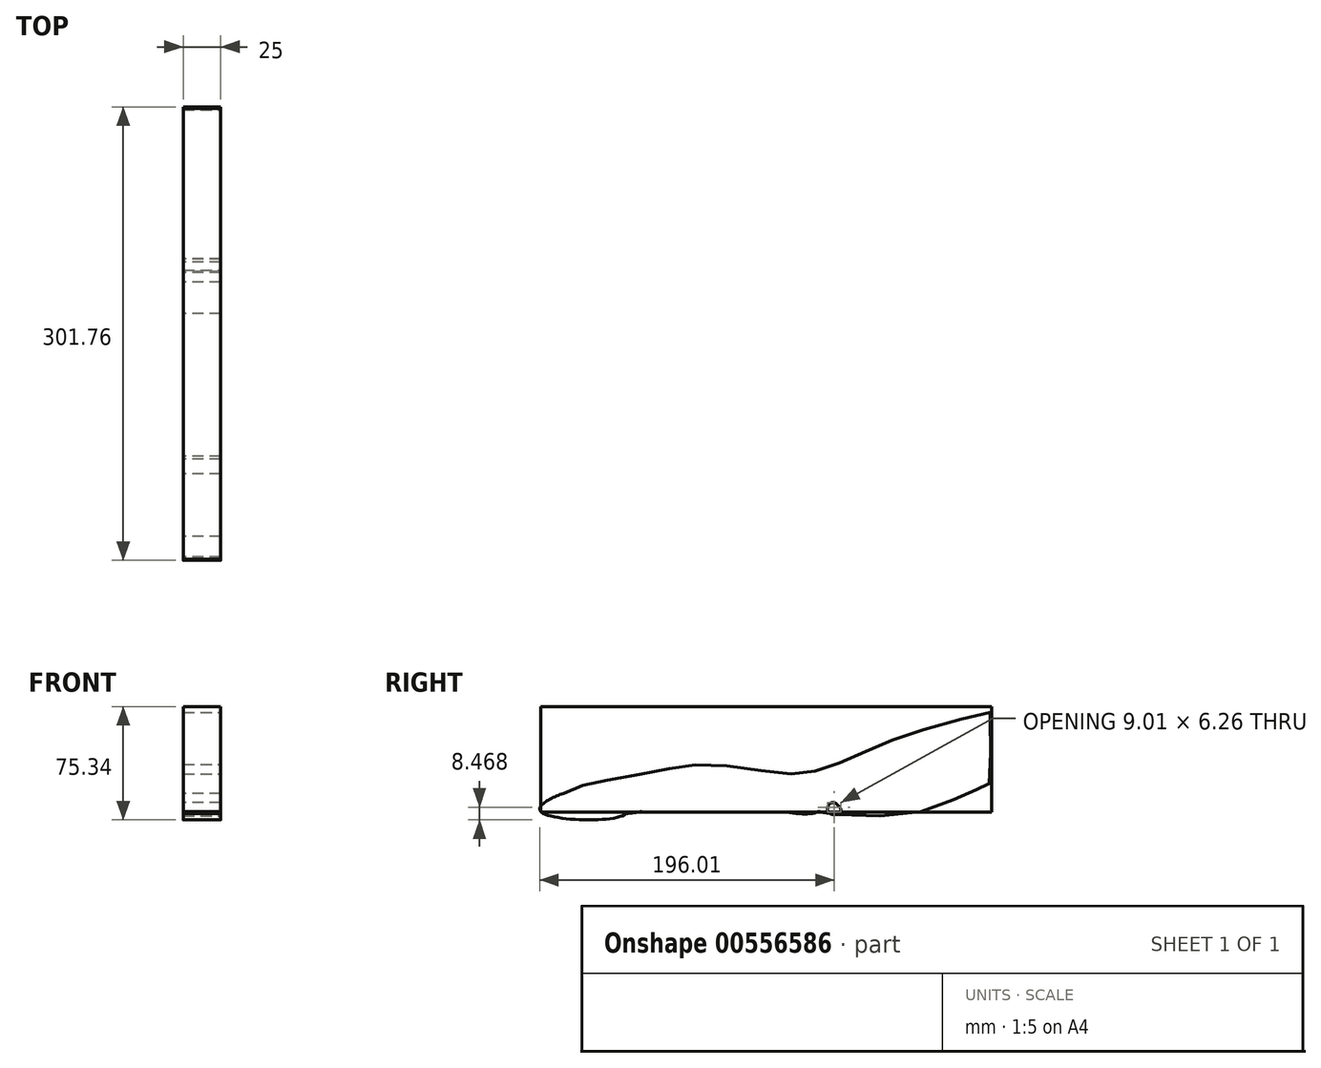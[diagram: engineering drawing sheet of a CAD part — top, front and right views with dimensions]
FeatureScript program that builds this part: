
annotation { "Feature Type Name" : "Feature", "Feature Type Description" : "" }
export const myFeature = defineFeature(function(context is Context, id is Id, definition is map)
    precondition{}
    {
        {
            var Q0;
            Q0=qCreatedBy(makeId("Right.planeOp"),FACE);
            var sketch = newSketch(context, id + "F0", { "sketchPlane" : qUnion([Q0])});
            skLineSegment(sketch, "E0.bottom", {"start": v(164.2, 50.84) * mm, "end": v(-135.8, 50.84) * mm});
            skLineSegment(sketch, "E0.top", {"start": v(164.2, -19.16) * mm, "end": v(-135.8, -19.16) * mm});
            skLineSegment(sketch, "E0.left", {"start": v(164.2, 50.84) * mm, "end": v(164.2, -19.16) * mm});
            skLineSegment(sketch, "E0.right", {"start": v(-135.8, 50.84) * mm, "end": v(-135.8, -19.16) * mm});
            skPoint(sketch, "E0.middle", {"position": v(14.2, 15.84) * mm});
            skSolve(sketch);
        }
        {
            var Q0;
            Q0=makeQuery(id+"F0.imprint","IMPRINT",FACE,{"disambiguationData":[TD([[makeQuery(id+"F0.imprint","IMPRINT",EDGE,{"derivedFrom":sQuery(id+"F0.wireOp",EDGE,"E0.bottom")}),1.0]])]});
            var sketch = newSketch(context, id + "F1", { "sketchPlane" : qUnion([Q0])});
            skSolve(sketch);
        }
        {
            var Q0;
            Q0=makeQuery(id+"F1.imprint","IMPRINT",FACE,{"disambiguationData":[TD([[makeQuery(id+"F1.imprint","IMPRINT",EDGE,{"derivedFrom":makeQuery(id+"F0.imprint","IMPRINT",EDGE,{"derivedFrom":sQuery(id+"F0.wireOp",EDGE,"E0.bottom")})}),1.0]])]});
            var sketch = newSketch(context, id + "F2", { "sketchPlane" : qUnion([Q0])});
            skFitSpline(sketch, "E1", {"points": [v(-135.83, -18.87) * mm, v(-120.6, -6.78) * mm, v(-101.8, 0) * mm, v(-59.7, 7.55) * mm, v(-26.1, 12.48) * mm, v(23.61, 6.66) * mm, v(50.49, 8.9) * mm, v(82.29, 21.89) * mm, v(125.28, 37.56) * mm, v(165.14, 46.97) * mm, v(163.8, 43.83) * mm, v(162.9, 0) * mm, v(154.84, -4.1) * mm, v(120.8, -17.98) * mm, v(48.7, -18.87) * mm, v(9.73, -11.7) * mm, v(-60.59, -17.53) * mm, v(-78.95, -20.22) * mm, v(-135.83, -18.87) * mm]});
            skFitSpline(sketch, "E2", {"points": [v(-120.6, -6.78) * mm, v(-135.83, -18.87) * mm, v(-78.95, -20.22) * mm, v(-90.15, -6.78) * mm, v(-120.6, -6.78) * mm]});
            skFitSpline(sketch, "E3", {"points": [v(9.73, -11.7) * mm, v(41.53, -6.78) * mm, v(48.7, -18.87) * mm, v(9.73, -11.7) * mm]});
            skFitSpline(sketch, "E4", {"points": [v(0, 0) * mm, v(38.4, 0) * mm, v(75.12, 6.66) * mm, v(116.32, 21.89) * mm, v(156.63, 33.98) * mm, v(156.19, 34.43) * mm, v(157.98, 34.87) * mm], "startDerivative": vector(170.88, -5.84) * mm, "endDerivative": vector(56.58, 7.65) * mm});
            skFitSpline(sketch, "E5", {"points": [v(50.49, -6.78) * mm, v(77.36, 0) * mm, v(118.56, 13.38) * mm, v(155.3, 18.75) * mm], "startDerivative": vector(86.35, 18.62) * mm, "endDerivative": vector(105.57, 9.52) * mm});
            skFitSpline(sketch, "E6", {"points": [v(-71.4, -17.53) * mm, v(-65.65, -18.4) * mm, v(-65.62, -10.51) * mm, v(-72.36, -10.51) * mm, v(-71.4, -17.53) * mm]});
            skFitSpline(sketch, "E7", {"points": [v(55.34, -18.87) * mm, v(57.75, -12.92) * mm, v(64.01, -17.53) * mm, v(62.09, -20.74) * mm, v(55.34, -18.87) * mm]});
            skSolve(sketch);
        }
        {
            var Q0;
            {var subQ0=sQuery(id+"F2.wireOp",EDGE,"E7");var subQ1=sQuery(id+"F2.wireOp",EDGE,"E1");var subQ2=makeQuery(id+"F2.imprint","INTERSECT",VERTEX,{"disambiguationData":[OD(0.0)],"derivedFrom":[subQ1,subQ0]});Q0=makeQuery(id+"F2.imprint","IMPRINT",FACE,{"disambiguationData":[TD([[makeQuery(id+"F2.imprint","IMPRINT",EDGE,{"disambiguationData":[TD([[subQ2,-1.0]])],"derivedFrom":subQ1}),1.0]])]});}
            var Q1;
            {var subQ0=sQuery(id+"F2.wireOp",EDGE,"E2");var subQ1=sQuery(id+"F2.wireOp",EDGE,"E1");var subQ2=makeQuery(id+"F2.imprint","INTERSECT",VERTEX,{"disambiguationData":[OD(1.0)],"derivedFrom":[subQ1,subQ0]});Q1=makeQuery(id+"F2.imprint","IMPRINT",FACE,{"disambiguationData":[TD([[makeQuery(id+"F2.imprint","IMPRINT",EDGE,{"disambiguationData":[TD([[subQ2,-1.0]])],"derivedFrom":subQ1}),1.0]])]});}
            var Q2;
            {var subQ0=sQuery(id+"F2.wireOp",EDGE,"E3");var subQ1=sQuery(id+"F2.wireOp",EDGE,"E1");var subQ2=makeQuery(id+"F2.imprint","INTERSECT",VERTEX,{"disambiguationData":[OD(0.0)],"derivedFrom":[subQ1,subQ0]});Q2=makeQuery(id+"F2.imprint","IMPRINT",FACE,{"disambiguationData":[TD([[makeQuery(id+"F2.imprint","IMPRINT",EDGE,{"disambiguationData":[TD([[subQ2,-1.0]])],"derivedFrom":subQ1}),-1.0]])]});}
            var Q3;
            {var subQ0=sQuery(id+"F2.wireOp",EDGE,"E6");var subQ1=sQuery(id+"F2.wireOp",EDGE,"E1");var subQ2=makeQuery(id+"F2.imprint","INTERSECT",VERTEX,{"disambiguationData":[OD(0.0)],"derivedFrom":[subQ1,subQ0]});Q3=makeQuery(id+"F2.imprint","IMPRINT",FACE,{"disambiguationData":[TD([[makeQuery(id+"F2.imprint","IMPRINT",EDGE,{"disambiguationData":[TD([[subQ2,-1.0]])],"derivedFrom":subQ1}),-1.0]])]});}
            var Q4;
            {var subQ0=sQuery(id+"F2.wireOp",EDGE,"E1");var subQ1=makeQuery(id+"F1.imprint","IMPRINT",EDGE,{"derivedFrom":makeQuery(id+"F0.imprint","IMPRINT",EDGE,{"derivedFrom":sQuery(id+"F0.wireOp",EDGE,"E0.left")})});var subQ2=makeQuery(id+"F2.imprint","INTERSECT",VERTEX,{"disambiguationData":[OD(0.0)],"derivedFrom":[subQ1,subQ0]});Q4=makeQuery(id+"F2.imprint","IMPRINT",FACE,{"disambiguationData":[TD([[makeQuery(id+"F2.imprint","IMPRINT",EDGE,{"disambiguationData":[TD([[subQ2,-1.0]])],"derivedFrom":subQ0}),-1.0]])]});}
            var Q5;
            {var subQ0=sQuery(id+"F2.wireOp",EDGE,"E3");var subQ1=makeQuery(id+"F1.imprint","IMPRINT",EDGE,{"derivedFrom":makeQuery(id+"F0.imprint","IMPRINT",EDGE,{"derivedFrom":sQuery(id+"F0.wireOp",EDGE,"E0.top")})});var subQ2=makeQuery(id+"F2.imprint","INTERSECT",VERTEX,{"disambiguationData":[OD(0.0)],"derivedFrom":[subQ1,subQ0]});Q5=makeQuery(id+"F2.imprint","IMPRINT",FACE,{"disambiguationData":[TD([[makeQuery(id+"F2.imprint","IMPRINT",EDGE,{"disambiguationData":[TD([[subQ2,-1.0]])],"derivedFrom":subQ0}),-1.0]])]});}
            var Q6;
            {var subQ0=sQuery(id+"F2.wireOp",EDGE,"E6");var subQ1=makeQuery(id+"F1.imprint","IMPRINT",EDGE,{"derivedFrom":makeQuery(id+"F0.imprint","IMPRINT",EDGE,{"derivedFrom":sQuery(id+"F0.wireOp",EDGE,"E0.top")})});var subQ2=makeQuery(id+"F2.imprint","INTERSECT",VERTEX,{"disambiguationData":[OD(0.0)],"derivedFrom":[subQ1,subQ0]});Q6=makeQuery(id+"F2.imprint","IMPRINT",FACE,{"disambiguationData":[TD([[makeQuery(id+"F2.imprint","IMPRINT",EDGE,{"disambiguationData":[TD([[subQ2,-1.0]])],"derivedFrom":subQ0}),1.0]])]});}
            var Q7;
            {var subQ0=sQuery(id+"F2.wireOp",EDGE,"E2");var subQ1=sQuery(id+"F2.wireOp",EDGE,"E1");var subQ2=makeQuery(id+"F2.imprint","INTERSECT",VERTEX,{"disambiguationData":[OD(0.0)],"derivedFrom":[subQ1,subQ0]});Q7=makeQuery(id+"F2.imprint","IMPRINT",FACE,{"disambiguationData":[TD([[makeQuery(id+"F2.imprint","IMPRINT",EDGE,{"disambiguationData":[TD([[subQ2,-1.0]])],"derivedFrom":subQ1}),1.0]])]});}
            var Q8;
            {var subQ0=sQuery(id+"F2.wireOp",EDGE,"E7");var subQ1=sQuery(id+"F2.wireOp",EDGE,"E1");var subQ2=makeQuery(id+"F2.imprint","INTERSECT",VERTEX,{"disambiguationData":[OD(0.0)],"derivedFrom":[subQ1,subQ0]});Q8=makeQuery(id+"F2.imprint","IMPRINT",FACE,{"disambiguationData":[TD([[makeQuery(id+"F2.imprint","IMPRINT",EDGE,{"disambiguationData":[TD([[subQ2,1.0]])],"derivedFrom":subQ1}),-1.0]])]});}
            var Q9;
            {var subQ0=sQuery(id+"F2.wireOp",EDGE,"E7");var subQ1=sQuery(id+"F2.wireOp",EDGE,"E1");var subQ2=makeQuery(id+"F2.imprint","INTERSECT",VERTEX,{"disambiguationData":[OD(1.0)],"derivedFrom":[subQ1,subQ0]});Q9=makeQuery(id+"F2.imprint","IMPRINT",FACE,{"disambiguationData":[TD([[makeQuery(id+"F2.imprint","IMPRINT",EDGE,{"disambiguationData":[TD([[subQ2,-1.0]])],"derivedFrom":subQ1}),-1.0]])]});}
            var Q10;
            {var subQ0=sQuery(id+"F2.wireOp",EDGE,"E2");var subQ1=sQuery(id+"F2.wireOp",EDGE,"E1");var subQ2=makeQuery(id+"F2.imprint","INTERSECT",VERTEX,{"disambiguationData":[OD(1.0)],"derivedFrom":[subQ1,subQ0]});Q10=makeQuery(id+"F2.imprint","IMPRINT",FACE,{"disambiguationData":[TD([[makeQuery(id+"F2.imprint","IMPRINT",EDGE,{"disambiguationData":[TD([[subQ2,1.0]])],"derivedFrom":subQ1}),-1.0]])]});}
            var Q11;
            {var subQ0=sQuery(id+"F2.wireOp",EDGE,"E2");var subQ1=sQuery(id+"F2.wireOp",EDGE,"E1");var subQ2=makeQuery(id+"F2.imprint","INTERSECT",VERTEX,{"disambiguationData":[OD(2.0)],"derivedFrom":[subQ1,subQ0]});Q11=makeQuery(id+"F2.imprint","IMPRINT",FACE,{"disambiguationData":[TD([[makeQuery(id+"F2.imprint","IMPRINT",EDGE,{"disambiguationData":[TD([[subQ2,-1.0]])],"derivedFrom":subQ1}),-1.0]])]});}
            var Q12;
            {var subQ0=sQuery(id+"F2.wireOp",EDGE,"E2");var subQ1=sQuery(id+"F2.wireOp",EDGE,"E1");var subQ2=makeQuery(id+"F2.imprint","INTERSECT",VERTEX,{"disambiguationData":[OD(0.0)],"derivedFrom":[subQ1,subQ0]});Q12=makeQuery(id+"F2.imprint","IMPRINT",FACE,{"disambiguationData":[TD([[makeQuery(id+"F2.imprint","IMPRINT",EDGE,{"disambiguationData":[TD([[subQ2,1.0]])],"derivedFrom":subQ1}),-1.0]])]});}
            var Q13;
            {var subQ0=sQuery(id+"F2.wireOp",EDGE,"E7");var subQ1=makeQuery(id+"F1.imprint","IMPRINT",EDGE,{"derivedFrom":makeQuery(id+"F0.imprint","IMPRINT",EDGE,{"derivedFrom":sQuery(id+"F0.wireOp",EDGE,"E0.top")})});var subQ2=makeQuery(id+"F2.imprint","INTERSECT",VERTEX,{"disambiguationData":[OD(0.0)],"derivedFrom":[subQ1,subQ0]});Q13=makeQuery(id+"F2.imprint","IMPRINT",FACE,{"disambiguationData":[TD([[makeQuery(id+"F2.imprint","IMPRINT",EDGE,{"disambiguationData":[TD([[subQ2,1.0]])],"derivedFrom":subQ0}),-1.0]])]});}
            var Q14;
            {var subQ0=sQuery(id+"F2.wireOp",EDGE,"E2");var subQ1=sQuery(id+"F2.wireOp",EDGE,"E1");var subQ2=makeQuery(id+"F2.imprint","INTERSECT",VERTEX,{"disambiguationData":[OD(0.0)],"derivedFrom":[subQ1,subQ0]});Q14=makeQuery(id+"F2.imprint","IMPRINT",FACE,{"disambiguationData":[TD([[makeQuery(id+"F2.imprint","IMPRINT",EDGE,{"disambiguationData":[TD([[subQ2,-1.0]])],"derivedFrom":subQ1}),-1.0]])]});}
            var Q15;
            {var subQ0=sQuery(id+"F2.wireOp",EDGE,"E2");var subQ1=sQuery(id+"F2.wireOp",EDGE,"E1");var subQ2=makeQuery(id+"F2.imprint","INTERSECT",VERTEX,{"disambiguationData":[OD(3.0)],"derivedFrom":[subQ1,subQ0]});Q15=makeQuery(id+"F2.imprint","IMPRINT",FACE,{"disambiguationData":[TD([[makeQuery(id+"F2.imprint","IMPRINT",EDGE,{"disambiguationData":[TD([[subQ2,1.0]])],"derivedFrom":subQ1}),1.0]])]});}
            var Q16;
            {var subQ0=sQuery(id+"F2.wireOp",EDGE,"E7");var subQ1=sQuery(id+"F2.wireOp",EDGE,"E1");var subQ2=makeQuery(id+"F2.imprint","INTERSECT",VERTEX,{"disambiguationData":[OD(0.0)],"derivedFrom":[subQ1,subQ0]});Q16=makeQuery(id+"F2.imprint","IMPRINT",FACE,{"disambiguationData":[TD([[makeQuery(id+"F2.imprint","IMPRINT",EDGE,{"disambiguationData":[TD([[subQ2,-1.0]])],"derivedFrom":subQ1}),-1.0]])]});}
            var Q17;
            {var subQ0=sQuery(id+"F2.wireOp",EDGE,"E3");var subQ1=sQuery(id+"F2.wireOp",EDGE,"E1");var subQ2=makeQuery(id+"F2.imprint","INTERSECT",VERTEX,{"disambiguationData":[OD(0.0)],"derivedFrom":[subQ1,subQ0]});Q17=makeQuery(id+"F2.imprint","IMPRINT",FACE,{"disambiguationData":[TD([[makeQuery(id+"F2.imprint","IMPRINT",EDGE,{"disambiguationData":[TD([[subQ2,-1.0]])],"derivedFrom":subQ1}),1.0]])]});}
            var Q18;
            {var subQ0=sQuery(id+"F2.wireOp",EDGE,"E6");var subQ1=sQuery(id+"F2.wireOp",EDGE,"E1");var subQ2=makeQuery(id+"F2.imprint","INTERSECT",VERTEX,{"disambiguationData":[OD(0.0)],"derivedFrom":[subQ1,subQ0]});Q18=makeQuery(id+"F2.imprint","IMPRINT",FACE,{"disambiguationData":[TD([[makeQuery(id+"F2.imprint","IMPRINT",EDGE,{"disambiguationData":[TD([[subQ2,-1.0]])],"derivedFrom":subQ1}),1.0]])]});}
            var Q19;
            {var subQ0=sQuery(id+"F2.wireOp",EDGE,"E2");var subQ1=sQuery(id+"F2.wireOp",EDGE,"E1");var subQ2=makeQuery(id+"F2.imprint","INTERSECT",VERTEX,{"disambiguationData":[OD(1.0)],"derivedFrom":[subQ1,subQ0]});Q19=makeQuery(id+"F2.imprint","IMPRINT",FACE,{"disambiguationData":[TD([[makeQuery(id+"F2.imprint","IMPRINT",EDGE,{"disambiguationData":[TD([[subQ2,-1.0]])],"derivedFrom":subQ1}),-1.0]])]});}
            var Q20;
            {var subQ0=sQuery(id+"F2.wireOp",EDGE,"E1");var subQ1=makeQuery(id+"F1.imprint","IMPRINT",EDGE,{"derivedFrom":makeQuery(id+"F0.imprint","IMPRINT",EDGE,{"derivedFrom":sQuery(id+"F0.wireOp",EDGE,"E0.top")})});var subQ2=makeQuery(id+"F2.imprint","INTERSECT",VERTEX,{"disambiguationData":[OD(3.0)],"derivedFrom":[subQ1,subQ0]});Q20=makeQuery(id+"F2.imprint","IMPRINT",FACE,{"disambiguationData":[TD([[makeQuery(id+"F2.imprint","IMPRINT",EDGE,{"disambiguationData":[TD([[subQ2,-1.0]])],"derivedFrom":subQ0}),-1.0]])]});}
            var Q21;
            {var subQ0=sQuery(id+"F2.wireOp",EDGE,"E2");var subQ4=sQuery(id+"F2.wireOp",EDGE,"E1");var subQ5=makeQuery(id+"F2.imprint","INTERSECT",VERTEX,{"disambiguationData":[OD(3.0)],"derivedFrom":[subQ4,subQ0]});Q21=makeQuery(id+"F2.imprint","IMPRINT",FACE,{"disambiguationData":[TD([[makeQuery(id+"F2.imprint","IMPRINT",EDGE,{"disambiguationData":[TD([[subQ5,1.0]])],"derivedFrom":subQ4}),-1.0]])]});}
            var Q22;
            {var subQ1=sQuery(id+"F2.wireOp",EDGE,"E1");var subQ6=sQuery(id+"F2.wireOp",EDGE,"E2");var subQ7=makeQuery(id+"F2.imprint","INTERSECT",VERTEX,{"disambiguationData":[OD(3.0)],"derivedFrom":[subQ1,subQ6]});Q22=makeQuery(id+"F2.imprint","IMPRINT",FACE,{"disambiguationData":[TD([[makeQuery(id+"F2.imprint","IMPRINT",EDGE,{"disambiguationData":[TD([[subQ7,-1.0]])],"derivedFrom":subQ1}),-1.0]])]});}
            var Q23;
            {var subQ0=sQuery(id+"F2.wireOp",EDGE,"E3");var subQ1=sQuery(id+"F2.wireOp",EDGE,"E1");var subQ2=makeQuery(id+"F2.imprint","INTERSECT",VERTEX,{"disambiguationData":[OD(1.0)],"derivedFrom":[subQ1,subQ0]});Q23=makeQuery(id+"F2.imprint","IMPRINT",FACE,{"disambiguationData":[TD([[makeQuery(id+"F2.imprint","IMPRINT",EDGE,{"disambiguationData":[TD([[subQ2,-1.0]])],"derivedFrom":subQ1}),1.0]])]});}
            var Q24;
            Q24=makeQuery(id+"F0.imprint","IMPRINT",FACE,{"disambiguationData":[TD([[makeQuery(id+"F0.imprint","IMPRINT",EDGE,{"derivedFrom":sQuery(id+"F0.wireOp",EDGE,"E0.bottom")}),1.0]])]});
            extrude(context, id + "F3", {"entities" : qUnion([Q0, Q1, Q2, Q3, Q4, Q5, Q6, Q7, Q8, Q9, Q10, Q11, Q12, Q13, Q14, Q15, Q16, Q17, Q18, Q19, Q20, Q21, Q22, Q23, Q24]), "depth" : 25 * mm, "offsetDistance" : 25 * mm});
        }
    });
